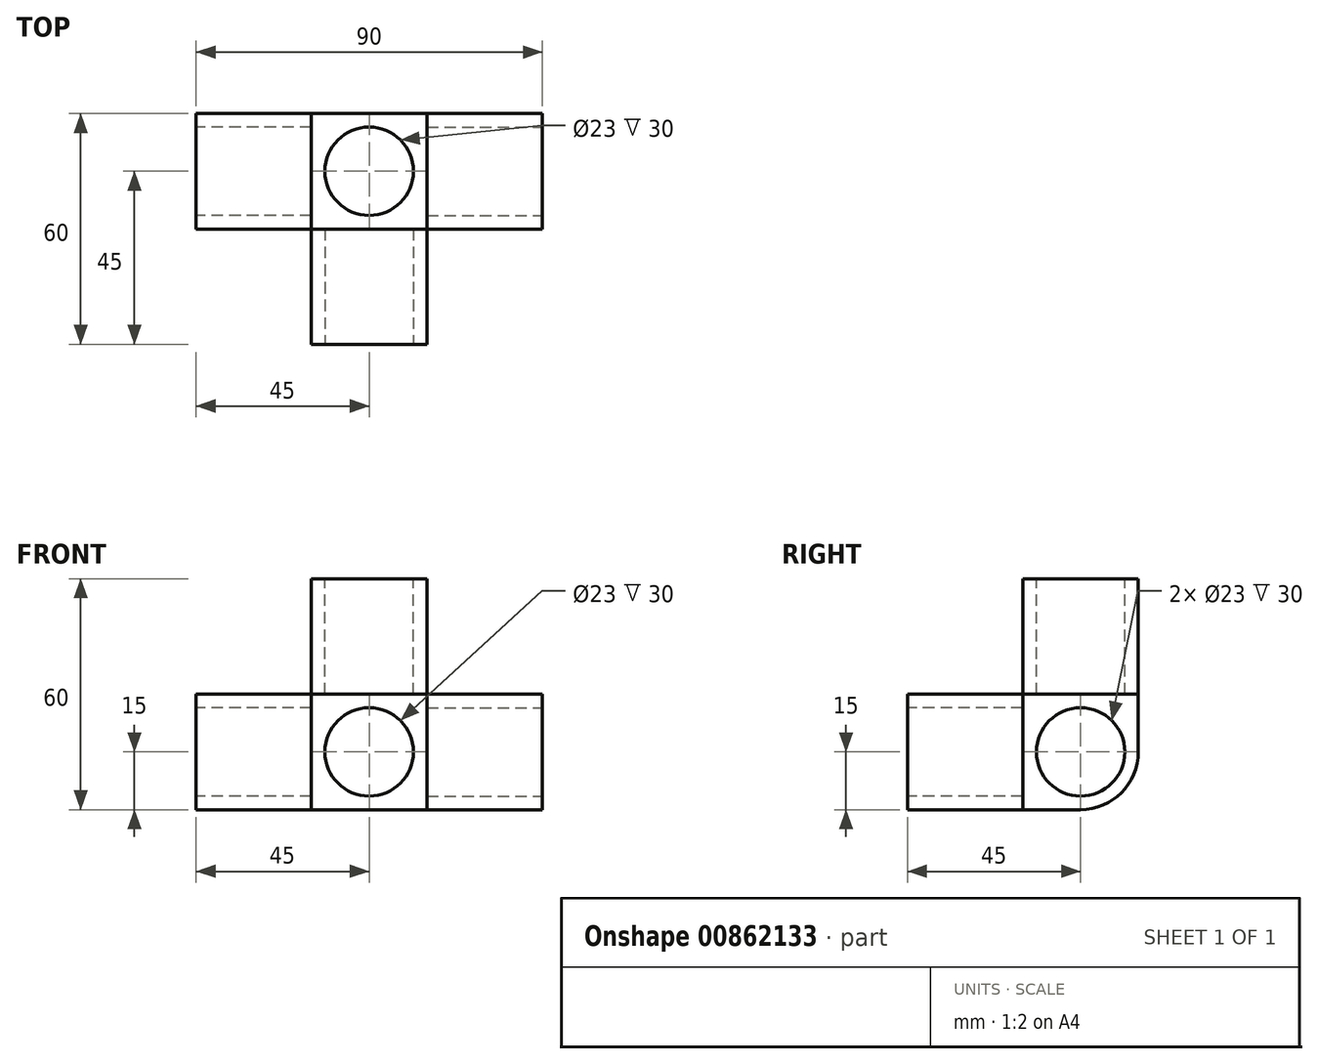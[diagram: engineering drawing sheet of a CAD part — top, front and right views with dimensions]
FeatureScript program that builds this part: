
annotation { "Feature Type Name" : "Feature", "Feature Type Description" : "" }
export const myFeature = defineFeature(function(context is Context, id is Id, definition is map)
    precondition{}
    {
        {
            var Q0;
            Q0=qCreatedBy(makeId("Top.planeOp"),FACE);
            var sketch = newSketch(context, id + "F0", { "sketchPlane" : qUnion([Q0])});
            skLineSegment(sketch, "E0.bottom", {"start": v(45, -15) * mm, "end": v(-45, -15) * mm});
            skLineSegment(sketch, "E0.top", {"start": v(45, 15) * mm, "end": v(-45, 15) * mm});
            skLineSegment(sketch, "E0.left", {"start": v(45, -15) * mm, "end": v(45, 15) * mm});
            skLineSegment(sketch, "E0.right", {"start": v(-45, -15) * mm, "end": v(-45, 15) * mm});
            skPoint(sketch, "E0.middle", {"position": v(0, 0) * mm});
            skLineSegment(sketch, "E1", {"start": v(-15, -15) * mm, "end": v(-15, -45) * mm});
            skLineSegment(sketch, "E2", {"start": v(-15, -45) * mm, "end": v(0, -45) * mm});
            skLineSegment(sketch, "E3.MirrorCS", {"start": v(15, -15) * mm, "end": v(15, -45) * mm});
            skLineSegment(sketch, "E4.MirrorCS", {"start": v(15, -45) * mm, "end": v(0, -45) * mm});
            skLineSegment(sketch, "E5", {"start": v(-15, -15) * mm, "end": v(-15, 15) * mm});
            skLineSegment(sketch, "E6", {"start": v(15, -15) * mm, "end": v(15, 15) * mm});
            skSolve(sketch);
        }
        {
            var Q0;
            {var subQ0=sQuery(id+"F0.wireOp",EDGE,"E0.right");Q0=makeQuery(id+"F0.imprint","IMPRINT",FACE,{"disambiguationData":[TD([[makeQuery(id+"F0.imprint","IMPRINT",EDGE,{"derivedFrom":subQ0}),-1.0]])]});}
            var Q1;
            {var subQ1=sQuery(id+"F0.wireOp",EDGE,"E1");Q1=makeQuery(id+"F0.imprint","IMPRINT",FACE,{"disambiguationData":[TD([[makeQuery(id+"F0.imprint","IMPRINT",EDGE,{"derivedFrom":subQ1}),1.0]])]});}
            var Q2;
            {var subQ0=sQuery(id+"F0.wireOp",EDGE,"E0.left");Q2=makeQuery(id+"F0.imprint","IMPRINT",FACE,{"disambiguationData":[TD([[makeQuery(id+"F0.imprint","IMPRINT",EDGE,{"derivedFrom":subQ0}),1.0]])]});}
            extrude(context, id + "F1", {"entities" : qUnion([Q0, Q1, Q2]), "depth" : 30 * mm, "offsetDistance" : 25 * mm});
        }
        {
            var Q0;
            {var subQ0=sQuery(id+"F0.wireOp",EDGE,"E5");Q0=makeQuery(id+"F0.imprint","IMPRINT",FACE,{"disambiguationData":[TD([[makeQuery(id+"F0.imprint","IMPRINT",EDGE,{"derivedFrom":subQ0}),-1.0]])]});}
            extrude(context, id + "F2", {"entities" : qUnion([Q0]), "depth" : 60 * mm, "offsetDistance" : 25 * mm});
        }
        {
            var Q0;
            Q0=makeQuery(id+"F2.opExtrude","CAP_FACE",FACE,{"disambiguationData":[OSD([sQuery(id+"F0.wireOp",EDGE,"E0.bottom"),sQuery(id+"F0.wireOp",EDGE,"E0.top"),sQuery(id+"F0.wireOp",EDGE,"E5"),sQuery(id+"F0.wireOp",EDGE,"E6")])],"isStart":false});
            var sketch = newSketch(context, id + "F3", { "sketchPlane" : qUnion([Q0])});
            skCircle(sketch, "E7", {"center": v(0, 0) * mm, "radius": 11.5 * mm});
            skSolve(sketch);
        }
        {
            var Q0;
            Q0=makeQuery(id+"F1.opExtrude","SWEPT_FACE",FACE,{"disambiguationData":[OSD([sQuery(id+"F0.wireOp",EDGE,"E2"),sQuery(id+"F0.wireOp",EDGE,"E4.MirrorCS")])]});
            var sketch = newSketch(context, id + "F4", { "sketchPlane" : qUnion([Q0])});
            skCircle(sketch, "E8", {"center": v(0, 15) * mm, "radius": 11.5 * mm});
            skPoint(sketch, "E8.centerSnap0", {"position": v(-15, 15) * mm});
            skPoint(sketch, "E8.centerSnap1", {"position": v(0, 0) * mm});
            skSolve(sketch);
        }
        {
            var Q0;
            Q0=makeQuery(id+"F1.opExtrude","SWEPT_FACE",FACE,{"disambiguationData":[OSD([sQuery(id+"F0.wireOp",EDGE,"E0.right")])]});
            var sketch = newSketch(context, id + "F5", { "sketchPlane" : qUnion([Q0])});
            skCircle(sketch, "E9", {"center": v(0, 15) * mm, "radius": 11.5 * mm});
            skPoint(sketch, "E9.centerSnap0", {"position": v(15, 15) * mm});
            skPoint(sketch, "E9.centerSnap1", {"position": v(0, 30) * mm});
            skSolve(sketch);
        }
        {
            var Q0;
            Q0=makeQuery(id+"F1.opExtrude","SWEPT_FACE",FACE,{"disambiguationData":[OSD([sQuery(id+"F0.wireOp",EDGE,"E0.left")])]});
            var sketch = newSketch(context, id + "F6", { "sketchPlane" : qUnion([Q0])});
            skCircle(sketch, "E10", {"center": v(0, 15) * mm, "radius": 11.5 * mm});
            skPoint(sketch, "E10.centerSnap0", {"position": v(-15, 15) * mm});
            skSolve(sketch);
        }
        {
            var Q0;
            Q0=makeQuery(id+"F3.imprint","IMPRINT",FACE,{"disambiguationData":[TD([[makeQuery(id+"F3.imprint","IMPRINT",EDGE,{"derivedFrom":sQuery(id+"F3.wireOp",EDGE,"E7")}),1.0]])]});
            extrude(context, id + "F7", {"entities" : qUnion([Q0]), "operationType" : NewBodyOperationType.REMOVE, "oppositeDirection" : true, "depth" : 30 * mm, "offsetDistance" : 25 * mm});
        }
        {
            var Q0;
            Q0=makeQuery(id+"F5.imprint","IMPRINT",FACE,{"disambiguationData":[TD([[makeQuery(id+"F5.imprint","IMPRINT",EDGE,{"derivedFrom":sQuery(id+"F5.wireOp",EDGE,"E9")}),1.0]])]});
            extrude(context, id + "F8", {"entities" : qUnion([Q0]), "operationType" : NewBodyOperationType.REMOVE, "oppositeDirection" : true, "depth" : 30 * mm, "offsetDistance" : 25 * mm});
        }
        {
            var Q0;
            Q0=makeQuery(id+"F4.imprint","IMPRINT",FACE,{"disambiguationData":[TD([[makeQuery(id+"F4.imprint","IMPRINT",EDGE,{"derivedFrom":sQuery(id+"F4.wireOp",EDGE,"E8")}),1.0]])]});
            extrude(context, id + "F9", {"entities" : qUnion([Q0]), "operationType" : NewBodyOperationType.REMOVE, "oppositeDirection" : true, "depth" : 30 * mm, "offsetDistance" : 25 * mm});
        }
        {
            var Q0;
            Q0=makeQuery(id+"F6.imprint","IMPRINT",FACE,{"disambiguationData":[TD([[makeQuery(id+"F6.imprint","IMPRINT",EDGE,{"derivedFrom":sQuery(id+"F6.wireOp",EDGE,"E10")}),1.0]])]});
            extrude(context, id + "F10", {"entities" : qUnion([Q0]), "operationType" : NewBodyOperationType.REMOVE, "oppositeDirection" : true, "depth" : 30 * mm, "offsetDistance" : 25 * mm});
        }
        {
            var Q0;
            {var subQ0=sQuery(id+"F0.wireOp",EDGE,"E0.top");Q0=makeQuery(id+"F1.opExtrude","CAP_EDGE",EDGE,{"disambiguationData":[OSD([subQ0]),TDD([makeQuery(id+"F0.imprint","IMPRINT",EDGE,{"disambiguationData":[TD([[makeQuery(id+"F0.imprint","INTERSECT",VERTEX,{"derivedFrom":[subQ0,sQuery(id+"F0.wireOp",EDGE,"E0.right")]}),1.0]])],"derivedFrom":subQ0})])],"isStart":true});}
            var Q1;
            Q1=makeQuery(id+"F2.opExtrude","CAP_EDGE",EDGE,{"disambiguationData":[OSD([sQuery(id+"F0.wireOp",EDGE,"E0.top")])],"isStart":true});
            var Q2;
            {var subQ0=sQuery(id+"F0.wireOp",EDGE,"E0.top");Q2=makeQuery(id+"F1.opExtrude","CAP_EDGE",EDGE,{"disambiguationData":[OSD([subQ0]),TDD([makeQuery(id+"F0.imprint","IMPRINT",EDGE,{"disambiguationData":[TD([[makeQuery(id+"F0.imprint","INTERSECT",VERTEX,{"derivedFrom":[subQ0,sQuery(id+"F0.wireOp",EDGE,"E0.left")]}),-1.0]])],"derivedFrom":subQ0})])],"isStart":true});}
            fillet(context, id + "F11", {"entities" : qUnion([Q0, Q1, Q2]), "radius" : 15 * mm, "tangentPropagation" : true, "allowEdgeOverflow" : false});
        }
    });
